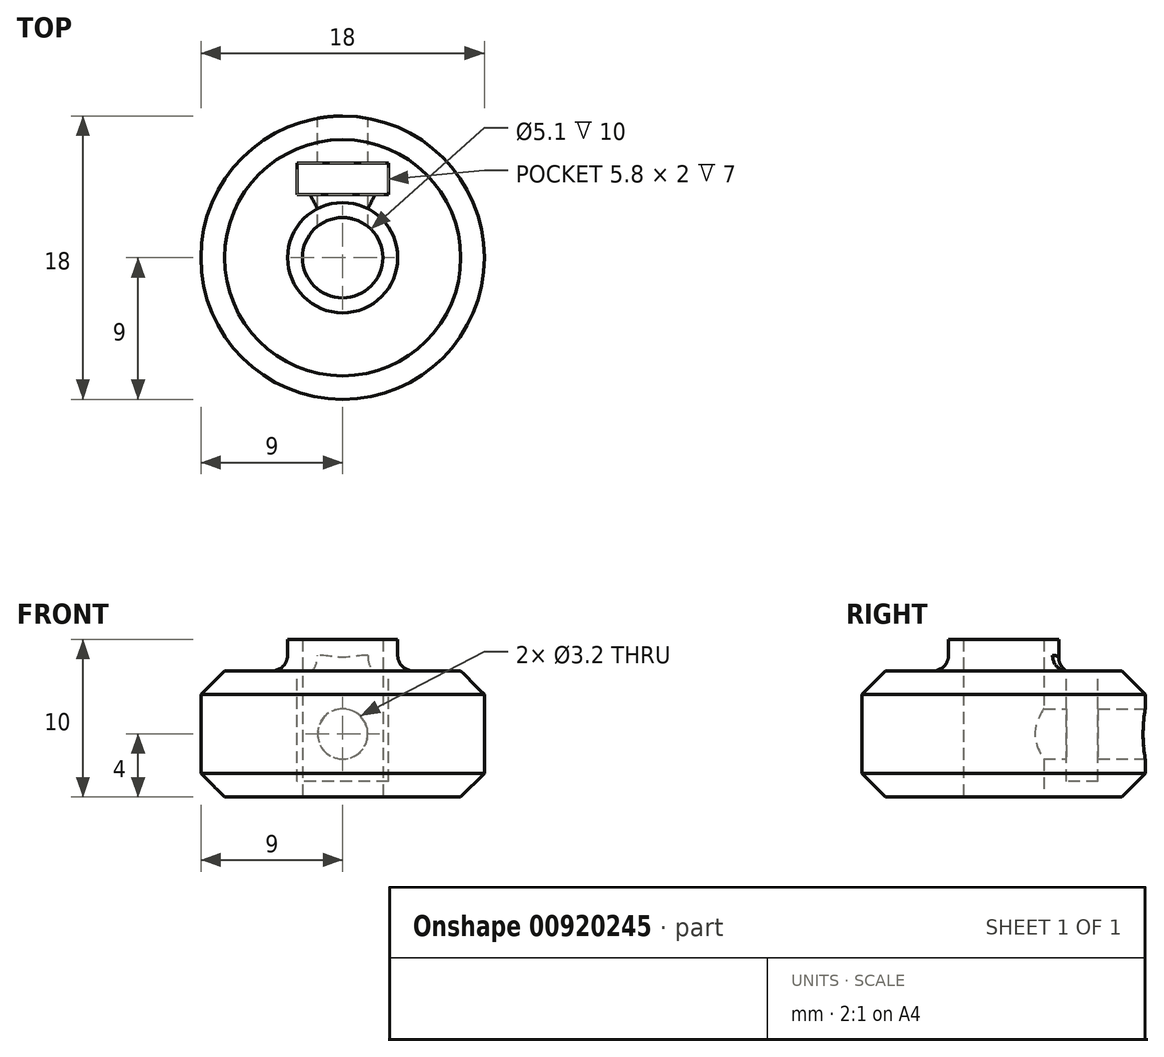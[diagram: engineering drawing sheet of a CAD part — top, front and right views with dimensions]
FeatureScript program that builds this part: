
annotation { "Feature Type Name" : "Feature", "Feature Type Description" : "" }
export const myFeature = defineFeature(function(context is Context, id is Id, definition is map)
    precondition{}
    {
        {
            var Q0;
            Q0=qCreatedBy(makeId("Front.planeOp"),FACE);
            var sketch = newSketch(context, id + "F0", { "sketchPlane" : qUnion([Q0])});
            skLineSegment(sketch, "E0", {"start": v(0, 0) * mm, "end": v(0, 20) * mm, "construction": true});
            skLineSegment(sketch, "E1", {"start": v(2.55, 0) * mm, "end": v(9, 0) * mm});
            skLineSegment(sketch, "E2", {"start": v(9, 0) * mm, "end": v(9, 8) * mm});
            skLineSegment(sketch, "E3", {"start": v(9, 8) * mm, "end": v(3.5, 8) * mm});
            skLineSegment(sketch, "E4", {"start": v(3.5, 8) * mm, "end": v(3.5, 10) * mm});
            skLineSegment(sketch, "E5", {"start": v(3.5, 10) * mm, "end": v(2.55, 10) * mm});
            skLineSegment(sketch, "E6", {"start": v(2.55, 10) * mm, "end": v(2.55, 0) * mm});
            skSolve(sketch);
        }
        {
            var Q0;
            Q0=qSketchRegion(id+"F0",true);
            var Q1;
            Q1=sQuery(id+"F0.wireOp",EDGE,"E0");
            revolve(context, id + "F1", {"surfaceOperationType" : NewSurfaceOperationType.NEW, "entities" : qUnion([Q0]), "axis" : qUnion([Q1]), "revolveType" : RevolveType.FULL});
        }
        {
            var Q0;
            Q0=makeQuery(id+"F1.opRevolve","SWEPT_FACE",FACE,{"disambiguationData":[OSD([sQuery(id+"F0.wireOp",EDGE,"E3")])]});
            var sketch = newSketch(context, id + "F2", { "sketchPlane" : qUnion([Q0])});
            skLineSegment(sketch, "E7", {"start": v(0, 0) * mm, "end": v(0, 16.53) * mm, "construction": true});
            skLineSegment(sketch, "E8.bottom", {"start": v(2.9, 6) * mm, "end": v(-2.9, 6) * mm});
            skLineSegment(sketch, "E8.top", {"start": v(2.9, 4) * mm, "end": v(-2.9, 4) * mm});
            skLineSegment(sketch, "E8.left", {"start": v(2.9, 6) * mm, "end": v(2.9, 4) * mm});
            skLineSegment(sketch, "E8.right", {"start": v(-2.9, 6) * mm, "end": v(-2.9, 4) * mm});
            skPoint(sketch, "E8.middle", {"position": v(0, 5) * mm});
            skSolve(sketch);
        }
        {
            var Q0;
            Q0=makeQuery(id+"F2.imprint","IMPRINT",FACE,{"disambiguationData":[TD([[makeQuery(id+"F2.imprint","IMPRINT",EDGE,{"derivedFrom":sQuery(id+"F2.wireOp",EDGE,"E8.bottom")}),1.0]])]});
            extrude(context, id + "F3", {"entities" : qUnion([Q0]), "operationType" : NewBodyOperationType.REMOVE, "oppositeDirection" : true, "depth" : 7 * mm, "offsetDistance" : 25 * mm});
        }
        {
            var Q0;
            Q0=qCreatedBy(makeId("Front.planeOp"),FACE);
            cPlane(context, id + "F4", {"entities" : qUnion([Q0]), "cplaneType" : CPlaneType.OFFSET, "offset" : 10 * mm, "oppositeDirection" : true, "width" : 150 * mm, "height" : 150 * mm});
        }
        {
            var Q0;
            Q0=qCreatedBy(id+"F4.planeOp",FACE);
            var sketch = newSketch(context, id + "F5", { "sketchPlane" : qUnion([Q0])});
            skLineSegment(sketch, "E9", {"start": v(0, 0) * mm, "end": v(0, 8) * mm, "construction": true});
            skCircle(sketch, "E10", {"center": v(0, 4) * mm, "radius": 1.6 * mm});
            skSolve(sketch);
        }
        {
            var Q0;
            Q0=makeQuery(id+"F5.imprint","IMPRINT",FACE,{"disambiguationData":[TD([[makeQuery(id+"F5.imprint","IMPRINT",EDGE,{"derivedFrom":sQuery(id+"F5.wireOp",EDGE,"E10")}),1.0]])]});
            var Q1;
            Q1=makeQuery(id+"F1.opRevolve","SWEPT_FACE",FACE,{"disambiguationData":[OSD([sQuery(id+"F0.wireOp",EDGE,"E6")])]});
            extrude(context, id + "F6", {"entities" : qUnion([Q0]), "operationType" : NewBodyOperationType.REMOVE, "endBound" : BoundingType.UP_TO_SURFACE, "depth" : 25 * mm, "endBoundEntityFace" : qUnion([Q1]), "offsetDistance" : 25 * mm});
        }
        {
            var Q0;
            Q0=makeQuery(id+"F1.opRevolve","SWEPT_EDGE",EDGE,{"disambiguationData":[OSD([sQuery(id+"F0.wireOp",EDGE,"E2"),sQuery(id+"F0.wireOp",EDGE,"E3")])]});
            var Q1;
            Q1=makeQuery(id+"F1.opRevolve","SWEPT_EDGE",EDGE,{"disambiguationData":[OSD([sQuery(id+"F0.wireOp",EDGE,"E1"),sQuery(id+"F0.wireOp",EDGE,"E2")])]});
            chamfer(context, id + "F7", {"entities" : qUnion([Q0, Q1]), "width" : 1.5 * mm, "tangentPropagation" : true});
        }
        {
            var Q0;
            Q0=makeQuery(id+"F1.opRevolve","SWEPT_EDGE",EDGE,{"disambiguationData":[OSD([sQuery(id+"F0.wireOp",EDGE,"E3"),sQuery(id+"F0.wireOp",EDGE,"E4")])]});
            fillet(context, id + "F8", {"entities" : qUnion([Q0]), "radius" : 1 * mm, "tangentPropagation" : true, "allowEdgeOverflow" : false});
        }
    });
